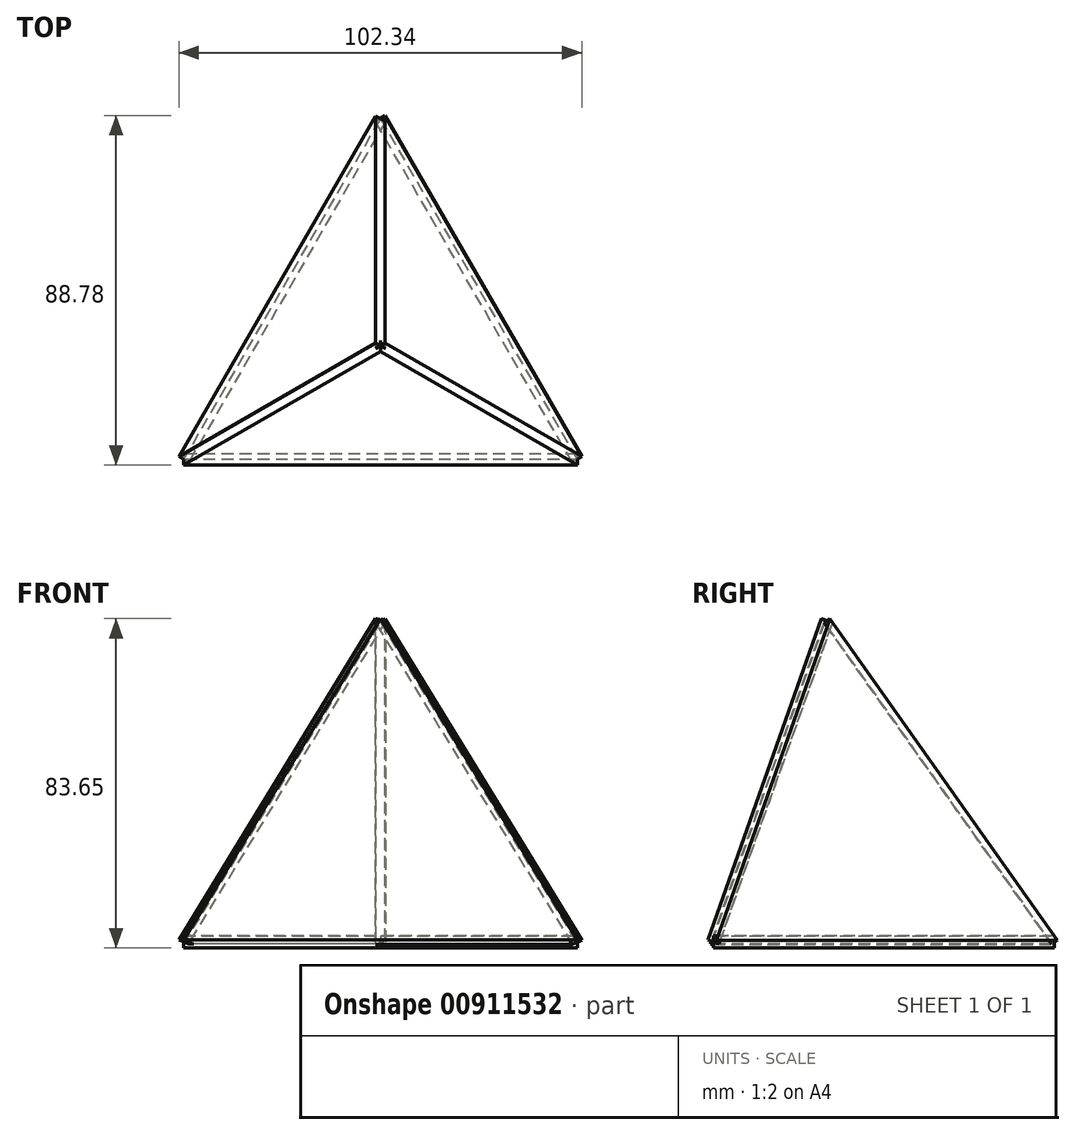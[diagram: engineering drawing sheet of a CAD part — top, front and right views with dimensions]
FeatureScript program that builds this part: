
annotation { "Feature Type Name" : "Feature", "Feature Type Description" : "" }
export const myFeature = defineFeature(function(context is Context, id is Id, definition is map)
    precondition{}
    {
        {
            var Q0;
            Q0=qCreatedBy(makeId("Top.planeOp"),FACE);
            var sketch = newSketch(context, id + "F0", { "sketchPlane" : qUnion([Q0])});
            skCircle(sketch, "E0.cCircle", {"center": v(0, 0) * mm, "radius": 28.87 * mm, "construction": true});
            skLineSegment(sketch, "E0.0", {"start": v(0, 57.74) * mm, "end": v(50, -28.87) * mm});
            skLineSegment(sketch, "E0.1", {"start": v(50, -28.87) * mm, "end": v(-50, -28.87) * mm});
            skLineSegment(sketch, "E0.2", {"start": v(-50, -28.87) * mm, "end": v(0, 57.74) * mm});
            skPoint(sketch, "E0.0.midPoint", {"position": v(25, 14.43) * mm});
            skSolve(sketch);
        }
        {
            var Q0;
            Q0=makeQuery(id+"F0.imprint","IMPRINT",FACE,{"disambiguationData":[TD([[makeQuery(id+"F0.imprint","IMPRINT",EDGE,{"derivedFrom":sQuery(id+"F0.wireOp",EDGE,"E0.0")}),-1.0]])]});
            extrude(context, id + "F1", {"entities" : qUnion([Q0]), "depth" : 3 * mm, "offsetDistance" : 25 * mm});
        }
        {
            var Q0;
            Q0=makeQuery(id+"F1.opExtrude","SWEPT_FACE",FACE,{"disambiguationData":[OSD([sQuery(id+"F0.wireOp",EDGE,"E0.1")])]});
            var sketch = newSketch(context, id + "F2", { "sketchPlane" : qUnion([Q0])});
            skLineSegment(sketch, "E1", {"start": v(-50, 1.5) * mm, "end": v(50, 1.5) * mm});
            skSolve(sketch);
        }
        {
            var Q0;
            Q0=makeQuery(id+"F1.opExtrude","SWEPT_BODY",BODY,{"disambiguationData":[OSD([sQuery(id+"F0.wireOp",EDGE,"E0.0"),sQuery(id+"F0.wireOp",EDGE,"E0.1"),sQuery(id+"F0.wireOp",EDGE,"E0.2")])]});
            transform(context, id + "F3", {"entities" : qUnion([Q0]), "transformType" : TransformType.TRANSLATION_3D, "dx" : 0 * mm, "dy" : 0 * mm, "dz" : 0 * mm, "makeCopy" : true});
        }
        {
            var Q0;
            Q0=makeQuery(id+"F3.opPattern","COPY",BODY,{"derivedFrom":makeQuery(id+"F1.opExtrude","SWEPT_BODY",BODY,{"disambiguationData":[OSD([sQuery(id+"F0.wireOp",EDGE,"E0.0"),sQuery(id+"F0.wireOp",EDGE,"E0.1"),sQuery(id+"F0.wireOp",EDGE,"E0.2")])]}),"instanceName":"1"});
            var Q1;
            Q1=sQuery(id+"F2.wireOp",EDGE,"E1");
            transform(context, id + "F4", {"entities" : qUnion([Q0]), "transformType" : TransformType.ROTATION, "transformAxis" : qUnion([Q1]), "angle" : 70.53 * degree, "makeCopy" : false});
        }
        {
            var Q0;
            Q0=makeQuery(id+"F3.opPattern","COPY",FACE,{"derivedFrom":makeQuery(id+"F1.opExtrude","SWEPT_FACE",FACE,{"disambiguationData":[OSD([sQuery(id+"F0.wireOp",EDGE,"E0.0")])]}),"instanceName":"1"});
            var sketch = newSketch(context, id + "F5", { "sketchPlane" : qUnion([Q0])});
            skLineSegment(sketch, "E2", {"start": v(-6.63, 72.6) * mm, "end": v(-35.77, -22.59) * mm});
            skPoint(sketch, "E2.startSnap0", {"position": v(-6.63, 73.03) * mm});
            skPoint(sketch, "E2.endSnap0", {"position": v(-35.9, -22.59) * mm});
            skSolve(sketch);
        }
        {
            var Q0;
            Q0=makeQuery(id+"F3.opPattern","COPY",BODY,{"derivedFrom":makeQuery(id+"F1.opExtrude","SWEPT_BODY",BODY,{"disambiguationData":[OSD([sQuery(id+"F0.wireOp",EDGE,"E0.0"),sQuery(id+"F0.wireOp",EDGE,"E0.1"),sQuery(id+"F0.wireOp",EDGE,"E0.2")])]}),"instanceName":"1"});
            transform(context, id + "F6", {"entities" : qUnion([Q0]), "transformType" : TransformType.TRANSLATION_3D, "dx" : 0 * mm, "dy" : 0 * mm, "dz" : 0 * mm, "makeCopy" : true});
        }
        {
            var Q0;
            Q0=makeQuery(id+"F6.opPattern","COPY",BODY,{"derivedFrom":makeQuery(id+"F3.opPattern","COPY",BODY,{"derivedFrom":makeQuery(id+"F1.opExtrude","SWEPT_BODY",BODY,{"disambiguationData":[OSD([sQuery(id+"F0.wireOp",EDGE,"E0.0"),sQuery(id+"F0.wireOp",EDGE,"E0.1"),sQuery(id+"F0.wireOp",EDGE,"E0.2")])]}),"instanceName":"1"}),"instanceName":"1"});
            var Q1;
            Q1=sQuery(id+"F5.wireOp",EDGE,"E2");
            var Q2;
            Q2=sQuery(id+"F5.wireOp",EDGE,"E2");
            transform(context, id + "F7", {"entities" : qUnion([Q0]), "transformType" : TransformType.ROTATION, "transformAxis" : qUnion([Q2]), "angle" : 70.53 * degree, "makeCopy" : false});
        }
        {
            var Q0;
            Q0=makeQuery(id+"F3.opPattern","COPY",FACE,{"derivedFrom":makeQuery(id+"F1.opExtrude","SWEPT_FACE",FACE,{"disambiguationData":[OSD([sQuery(id+"F0.wireOp",EDGE,"E0.2")])]}),"instanceName":"1"});
            var sketch = newSketch(context, id + "F8", { "sketchPlane" : qUnion([Q0])});
            skLineSegment(sketch, "E3", {"start": v(35.9, -22.59) * mm, "end": v(6.63, 73.03) * mm});
            skSolve(sketch);
        }
        {
            var Q0;
            Q0=makeQuery(id+"F6.opPattern","COPY",BODY,{"derivedFrom":makeQuery(id+"F3.opPattern","COPY",BODY,{"derivedFrom":makeQuery(id+"F1.opExtrude","SWEPT_BODY",BODY,{"disambiguationData":[OSD([sQuery(id+"F0.wireOp",EDGE,"E0.0"),sQuery(id+"F0.wireOp",EDGE,"E0.1"),sQuery(id+"F0.wireOp",EDGE,"E0.2")])]}),"instanceName":"1"}),"instanceName":"1"});
            transform(context, id + "F9", {"entities" : qUnion([Q0]), "transformType" : TransformType.TRANSLATION_3D, "dx" : 0 * mm, "dy" : 0 * mm, "dz" : 0 * mm, "makeCopy" : true});
        }
        {
            var Q0;
            Q0=makeQuery(id+"F3.opPattern","COPY",BODY,{"derivedFrom":makeQuery(id+"F1.opExtrude","SWEPT_BODY",BODY,{"disambiguationData":[OSD([sQuery(id+"F0.wireOp",EDGE,"E0.0"),sQuery(id+"F0.wireOp",EDGE,"E0.1"),sQuery(id+"F0.wireOp",EDGE,"E0.2")])]}),"instanceName":"1"});
            transform(context, id + "F10", {"entities" : qUnion([Q0]), "transformType" : TransformType.TRANSLATION_3D, "dx" : 0 * mm, "dy" : 0 * mm, "dz" : 0 * mm, "makeCopy" : true});
        }
        {
            var Q0;
            Q0=makeQuery(id+"F10.opPattern","COPY",BODY,{"derivedFrom":makeQuery(id+"F3.opPattern","COPY",BODY,{"derivedFrom":makeQuery(id+"F1.opExtrude","SWEPT_BODY",BODY,{"disambiguationData":[OSD([sQuery(id+"F0.wireOp",EDGE,"E0.0"),sQuery(id+"F0.wireOp",EDGE,"E0.1"),sQuery(id+"F0.wireOp",EDGE,"E0.2")])]}),"instanceName":"1"}),"instanceName":"1"});
            var Q1;
            Q1=sQuery(id+"F8.wireOp",EDGE,"E3");
            var Q2;
            Q2=sQuery(id+"F8.wireOp",EDGE,"E3");
            transform(context, id + "F11", {"entities" : qUnion([Q0]), "transformType" : TransformType.ROTATION, "transformAxis" : qUnion([Q2]), "angle" : 70.53 * degree, "makeCopy" : false});
        }
    });
